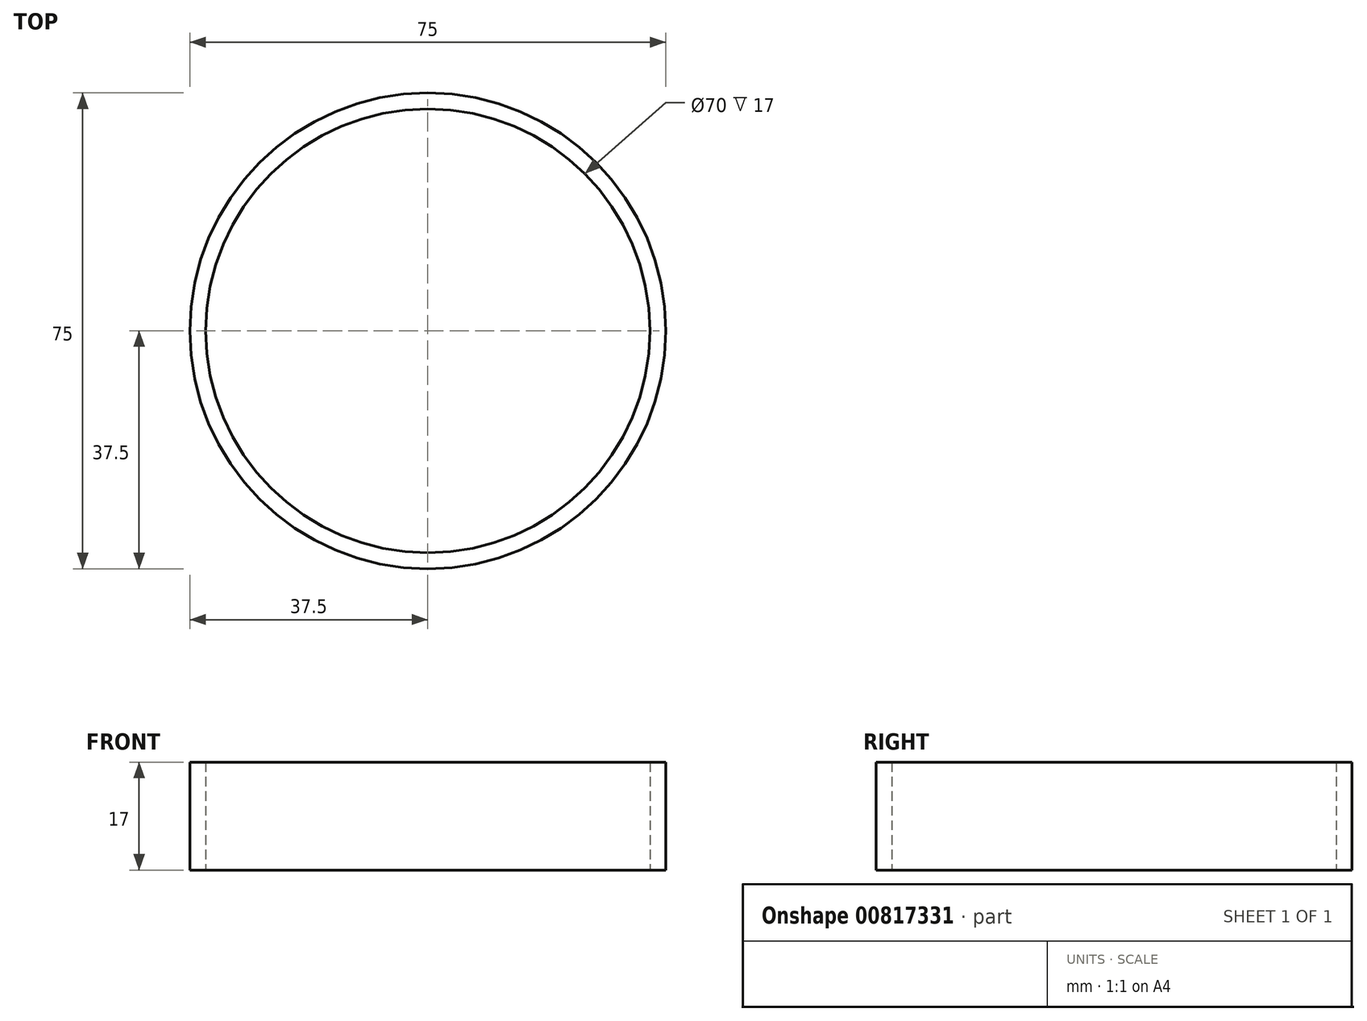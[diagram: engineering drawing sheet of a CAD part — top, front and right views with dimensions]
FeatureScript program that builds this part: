
annotation { "Feature Type Name" : "Feature", "Feature Type Description" : "" }
export const myFeature = defineFeature(function(context is Context, id is Id, definition is map)
    precondition{}
    {
        {
            var Q0;
            Q0=qCreatedBy(makeId("Top.planeOp"),FACE);
            var sketch = newSketch(context, id + "F0", { "sketchPlane" : qUnion([Q0])});
            skCircle(sketch, "E0", {"center": v(0, 0) * mm, "radius": 35 * mm});
            skCircle(sketch, "E1.0", {"center": v(0, 0) * mm, "radius": 37.5 * mm});
            skSolve(sketch);
        }
        {
            var Q0;
            Q0 = qSketchRegion(id + "F0", true);
            extrude(context, id + "F1", {"entities" : qUnion([Q0]), "depth" : 17 * mm, "offsetDistance" : 25.4 * mm});
        }
    });
